# Revit family: Heat_Pump-Packaged_Rooftop-York-XP036-060-(3-5Ton)
name_source: partatom
category: Mechanical Equipment
units: mm (PartAtom-declared; Revit-internal decimal feet)

## family parameters
Always vertical = Yes
Cut with Voids When Loaded = No
Maintain Annotation Orientation = No
Part Type = Normal
Room Calculation Point = No
Round Connector Dimension = Use Radius
Shared = No
Work Plane-Based = No

## types (1)
- 3 Ton - Electric Heat - 208V
    Assembly Code = D3060300
    Belt Drive Evaporator Fan RPM = 1725
    Belt Drive Evaporator Fan Type = Centrifugal
    Clearance Offset Front = 24"
    Clearance Offset Right = 24"
    Clearance Offset Top = 72"
    Compressor Locked Rotor Current = 0 A
    Compressor Maximum Continuous Current = 0 A
    Compressor Quantity = 1
    Compressor Running Load Current = 0 A
    Compressor Type = Scroll
    Condensate Drain Connection Description = Condensate Drain
    Condensate Drain Connection Diameter = 1"
    Condensate Drain Radius = 3/8"
    Condenser Coil Fins per Inch = 18
    Condenser Coil Material = Metal - JCI - Aluminum Micro Channel
    Condenser Coil Row Count = 2
    Condenser Fan Drive Type = Direct Drive
    Condenser Fan Horsepower = 0.37 kW
    Condenser Fan Type = Prop
    Control Connection Description = Control Wiring
    Convenience Outlet Electrical Connection Description = Convenience Outlet Power
    Convenience Outlet Full Load Current = 0 A
    Convenience Outlet Voltage = 110 V
    Curb Length = 73"
    Curb Material = Metal - JCI - Galvanized Steel w Wood Nailer
    Curb Width = 37 1/4"
    Default Elevation = 0"
    Description = Air Handling Unit, Commercial Comfort Systems, Series 5, Electrical, 3 to 5 Ton Unit
    Direct Drive Evaporator Fan RPM = 1050
    Direct Drive Evaporator Fan Type = Centrifugal
    Economizer Operating Weight = 50.00 lb
    Electric Heat Current = 0 A
    Electric Heat Operating Weight = 28.00 lb
    Electric Heat Wattage = 0 W
    Electrical Connection Description = Equipment Power
    Energy Efficiency Rating = 11
    Evaporator Coil Fins per Inch = 13
    Evaporator Coil Row Count = 4
    Evaporator Refrigerant Control = TXV
    Family Revision Date = 06/10/2010
    Filter Size and Quantity = 15x20-2, 14x25-1
    Frame Finish = Paint - JCI - Powder - Champagne
    Frame Material = Metal - JCI - Steel - Galvanized
    Frequency = 60 Hz
    Heating Seasonal Performance Factor = 7.7
    Height = 32 5/8"
    Keynote = 15700
    Length = 82 1/4"
    Manufacturer = Johnson Controls, Inc.
    Maximum Applied Voltage = 0 V
    Maximum Overcurrent Protection = 0 A
    Minimum Applied Voltage = 0 V
    Minimum Circuit Current = 0 A
    Model = J04XP, Electric, Slab Mount
    Nominal Air Flow = 1200 CFM
    Nominal Cooling Capacity = 5.0 ton
    Number of Poles = 1
    OD Fan Motor Full Load Current = 0 A
    OmniClass Number = 23.75.10.24.21.27.11
    OmniClass Title = Packaged Air Conditioners
    Operating Weight = 575.00 lb
    Power Exhaust Operating Weight = 50.00 lb
    Power Factor = 1
    Product Documentation Link = http://www.johnsoncontrols.com
    Product Page URL = http://www.johnsoncontrols.com
    Refrigerant Charge = 13.00 lb
    Refrigerant Used = R-410A
    Return Air Connection Description = Return Air
    Seasonal Energy Efficiency Rating = 13
    Supply Air Connection Description = Supply Air
    Supply Fan Full Load Current = 0 A
    URL = http://www.johnsoncontrols.com
    Voltage = 0 V
    Width = 44 7/8"

## geometry (parser evidence)
native form markers: Sweep x27
no freeform markers — native parametric forms only
